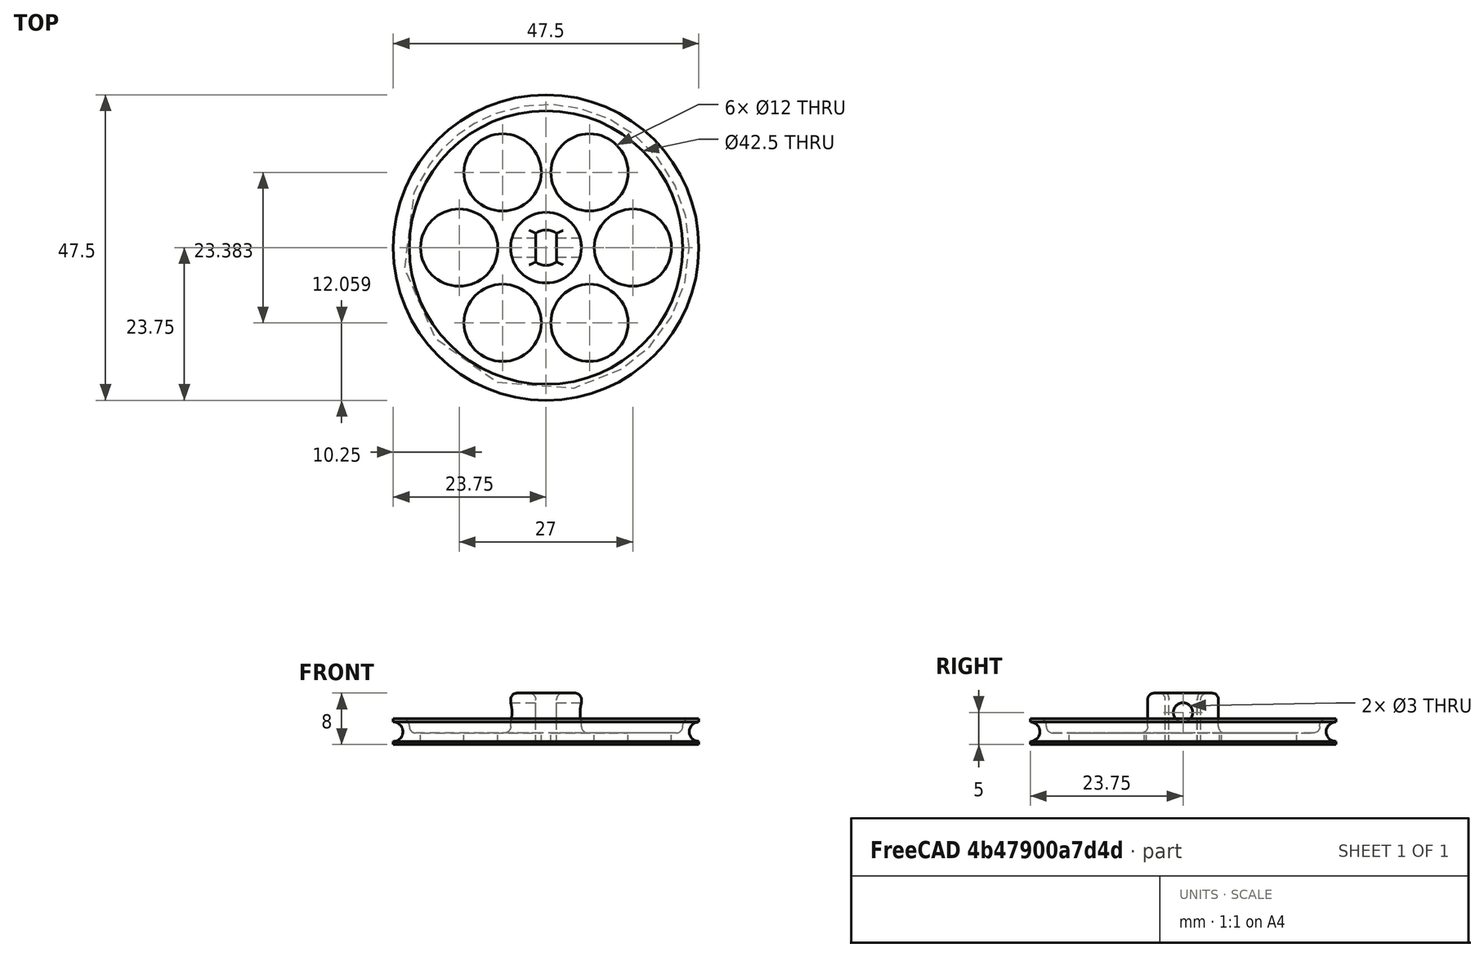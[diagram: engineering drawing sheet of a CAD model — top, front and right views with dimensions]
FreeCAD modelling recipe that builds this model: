
FCSTD DOCUMENT  (FreeCAD 0.16R6712 (Git))
Label: wheel47
License: All rights reserved
LicenseURL: http://en.wikipedia.org/wiki/All_rights_reserved
objects: Part::Cylinder×6, Part::Cut×5, PartDesign::Fillet×5, Sketcher::SketchObject×1, Part::Torus×1, Part::Box×1, Part::MultiCommon×1, Part::FeaturePython×1, Drawing::FeaturePage×1, Part::MultiFuse×1, Spreadsheet::Sheet×1
note: 22 computed .brp shape members not serialized (recipe doc carries the construction recipe); baked Part::Feature solids carry a one-line shape summary decoded from their .brp

FEATURE [Sketcher::SketchObject] Sketch
FEATURE [Part::Torus] Torus
  Angle1 = -180
  Angle2 = 180
  Angle3 = 360
  Placement = pos=(0,0,2) rot=(0,0,1;0rad)
  Radius1 = 23.75
  Radius2 = 1.5
  expr: Radius1 = data.wheel_radius
FEATURE [Part::Cylinder] Cylinder
  Angle = 360
  Height = 4
  Placement = pos=(0,0,0) rot=(0,0,0;0.012796rad)
  Radius = 23.75
  expr: Height = data.rim_thickness
  expr: Radius = data.wheel_radius
FEATURE [Part::Cut] Cut  label="rim"
  Base = -> Cylinder
  Tool = -> Torus
FEATURE [Part::Cylinder] Cylinder001  label="hub"
  Angle = 360
  Height = 8
  Radius = 5.5
FEATURE [Part::Cylinder] Cylinder002  label="Cylinder001"
  Angle = 360
  Height = 12
  Radius = 2.75
FEATURE [Part::Box] Box  label="Cube"
  Height = 12
  Length = 3.25
  Placement = pos=(-1.6125,-6,0) rot=(0,0,1;0rad)
  Width = 12
FEATURE [Part::MultiCommon] Common  label="shaft"
  Shapes = -> [Box,Cylinder002]
FEATURE [Part::Cylinder] Cylinder003  label="setscrew"
  Angle = 360
  Height = 20
  Placement = pos=(-10,0,5) rot=(0,1,0;1.5708rad)
  Radius = 1.5
FEATURE [Part::Cylinder] Cylinder004  label="spoke"
  Angle = 360
  Height = 20
  Placement = pos=(13.5,0,0) rot=(0,0,1;0rad)
  Radius = 6
FEATURE [Part::FeaturePython] Array  # Draft array (typed FeaturePython)
  Angle = 360
  ArrayType = 1
  Axis = (0,0,1)
  Base = -> Cylinder004
  Center = (0,0,0)
  Fuse = false
  IntervalAxis = (0,0,0)
  IntervalX = (1,0,0)
  IntervalY = (0,1,0)
  IntervalZ = (0,0,0)
  NumberPolar = 6
  NumberX = 1
  NumberY = 2
  NumberZ = 1
FEATURE [Drawing::FeaturePage] Page
  EditableTexts = AUTHOR NAME | CREATION DATE | SUPERVISOR NAME | CHECK DATE | SCALE | WEIGHT | NUMBER | SHEET | TITLE | SUBTITLE
FEATURE [Part::Cylinder] Cylinder005  label="Cylinder002"
  Angle = 360
  Height = 10
  Placement = pos=(0,0,1.8) rot=(0,0,1;0rad)
  Radius = 21.25
  expr: Radius = data.wheel_radius - 2.5mm
FEATURE [Part::Cut] Cut002
  Base = -> Cut
  Tool = -> Cylinder005
FEATURE [Part::MultiFuse] Fusion
  Shapes = -> [Cylinder001,Cut002]
FEATURE [Part::Cut] Cut003
  Base = -> Fusion
  Tool = -> Common
FEATURE [Part::Cut] Cut004
  Base = -> Cut003
  Tool = -> Cylinder003
FEATURE [Part::Cut] Cut005
  Base = -> Cut004
  Tool = -> Array
FEATURE [Spreadsheet::Sheet] Spreadsheet  label="data"
  cells = A3=wheel_diameter; B3(wheel_diameter)==47.5mm
FEATURE [PartDesign::Fillet] Fillet
  Base = -> Cut005 [Edge4,Edge3,Edge2,Edge5]
  Radius = 1
FEATURE [PartDesign::Fillet] Fillet002
  Base = -> Fillet [Edge35]
  Radius = 1
FEATURE [PartDesign::Fillet] Fillet003
  Base = -> Fillet002 [Edge35]
  Radius = 1
FEATURE [PartDesign::Fillet] Fillet004
  Base = -> Fillet003 [Edge13]
  Radius = 1
FEATURE [PartDesign::Fillet] Fillet005
  Base = -> Fillet004 [Edge31]
  Radius = 1
